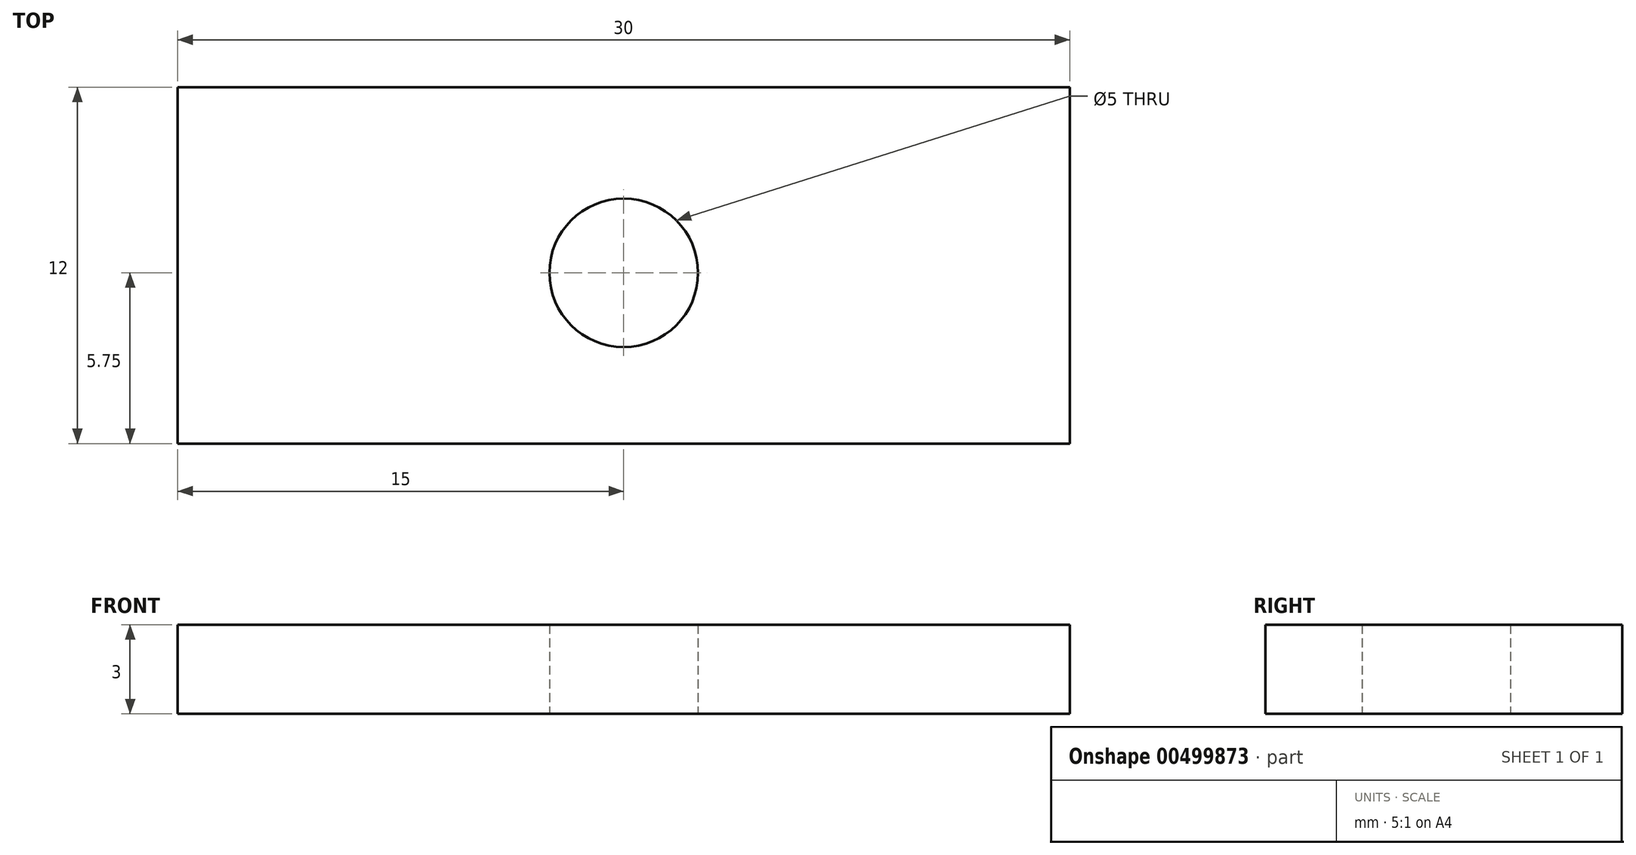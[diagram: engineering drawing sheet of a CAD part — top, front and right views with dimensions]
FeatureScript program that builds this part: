
annotation { "Feature Type Name" : "Feature", "Feature Type Description" : "" }
export const myFeature = defineFeature(function(context is Context, id is Id, definition is map)
    precondition{}
    {
        {
            var Q0;
            Q0=qCreatedBy(makeId("Top.planeOp"),FACE);
            var sketch = newSketch(context, id + "F0", { "sketchPlane" : qUnion([Q0])});
            skLineSegment(sketch, "E0.bottom", {"start": v(15, -6) * mm, "end": v(-15, -6) * mm});
            skLineSegment(sketch, "E0.top", {"start": v(15, 6) * mm, "end": v(-15, 6) * mm});
            skLineSegment(sketch, "E0.left", {"start": v(15, -6) * mm, "end": v(15, 6) * mm});
            skLineSegment(sketch, "E0.right", {"start": v(-15, -6) * mm, "end": v(-15, 6) * mm});
            skPoint(sketch, "E0.middle", {"position": v(0, 0) * mm});
            skCircle(sketch, "E1", {"center": v(0, -0.25) * mm, "radius": 2.5 * mm});
            skSolve(sketch);
        }
        {
            var Q0;
            Q0 = qSketchRegion(id + "F0", true);
            extrude(context, id + "F1", {"entities" : qUnion([Q0]), "depth" : 3 * mm, "offsetDistance" : 25 * mm});
        }
    });
